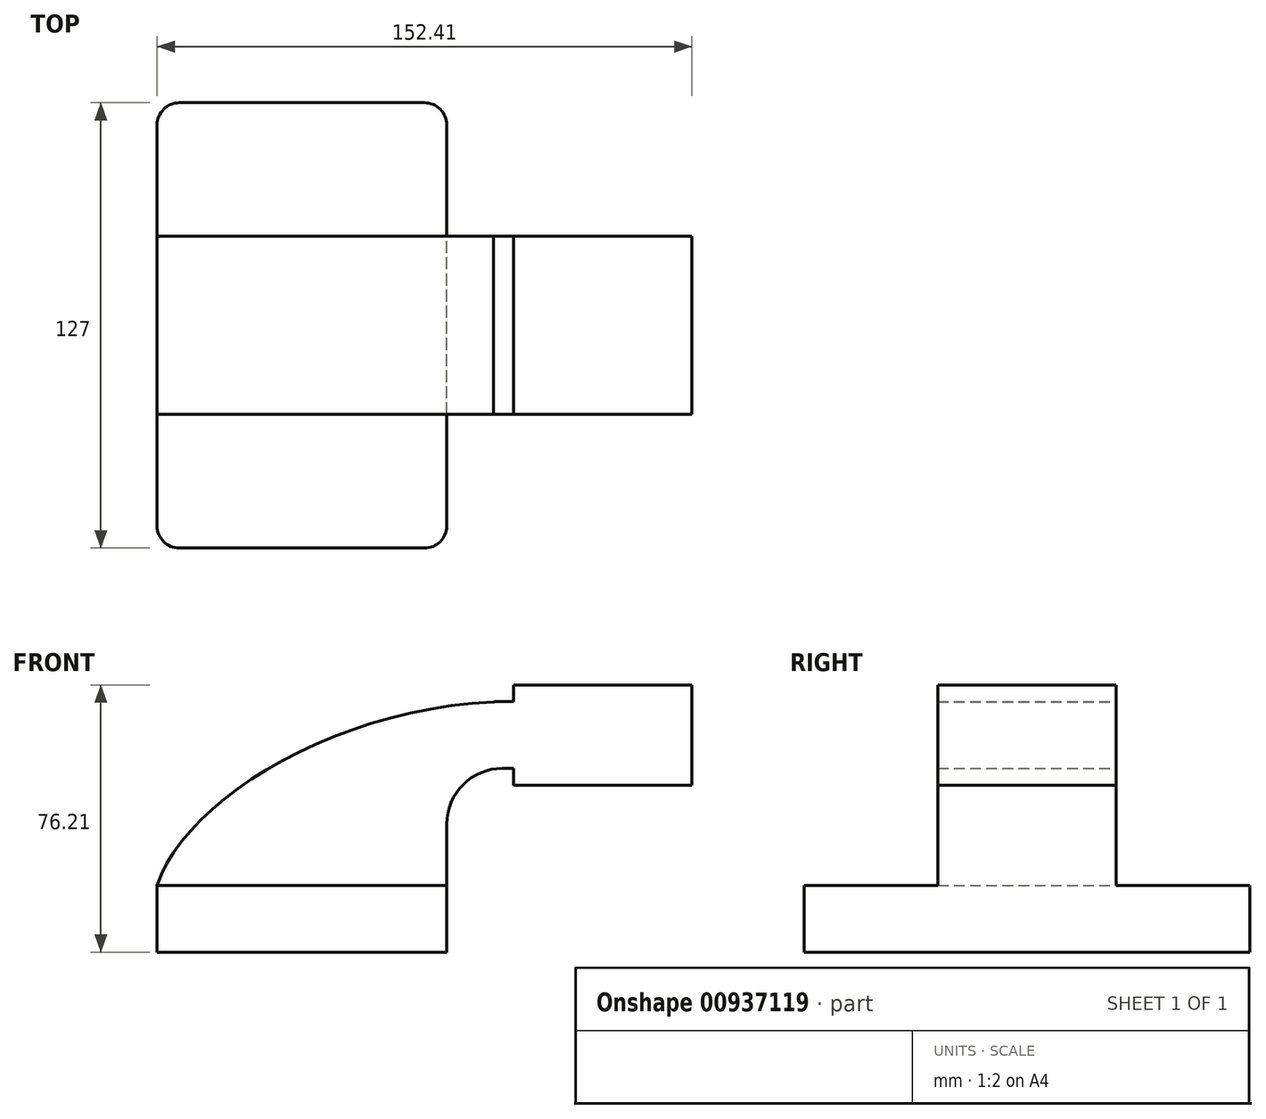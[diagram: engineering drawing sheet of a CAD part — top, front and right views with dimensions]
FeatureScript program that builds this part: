
annotation { "Feature Type Name" : "Feature", "Feature Type Description" : "" }
export const myFeature = defineFeature(function(context is Context, id is Id, definition is map)
    precondition{}
    {
        {
            var Q0;
            Q0=qCreatedBy(makeId("Front.planeOp"),FACE);
            var sketch = newSketch(context, id + "F0", { "sketchPlane" : qUnion([Q0])});
            skLineSegment(sketch, "E0.bottom", {"start": v(-41.28, -9.53) * mm, "end": v(41.28, -9.53) * mm});
            skLineSegment(sketch, "E0.top", {"start": v(-41.28, 9.53) * mm, "end": v(41.28, 9.53) * mm});
            skLineSegment(sketch, "E0.left", {"start": v(-41.28, -9.53) * mm, "end": v(-41.28, 9.53) * mm});
            skLineSegment(sketch, "E0.right", {"start": v(41.28, -9.53) * mm, "end": v(41.28, 9.53) * mm});
            skPoint(sketch, "E0.middle", {"position": v(0, 0) * mm});
            skLineSegment(sketch, "E1.bottom", {"start": v(60.33, 38.1) * mm, "end": v(111.12, 38.1) * mm});
            skLineSegment(sketch, "E1.top", {"start": v(60.33, 66.67) * mm, "end": v(111.12, 66.67) * mm});
            skLineSegment(sketch, "E1.left", {"start": v(60.33, 38.1) * mm, "end": v(60.33, 66.67) * mm});
            skLineSegment(sketch, "E1.right", {"start": v(111.12, 38.1) * mm, "end": v(111.12, 66.67) * mm});
            skPoint(sketch, "E1.middle", {"position": v(85.72, 52.39) * mm});
            skLineSegment(sketch, "E2", {"start": v(41.28, 9.53) * mm, "end": v(41.28, 27) * mm});
            skArc(sketch, "E3", {"start": v(41.27, 27) * mm, "mid": v(45.92, 38.23) * mm, "end": v(57.15, 42.88) * mm});
            skLineSegment(sketch, "E4", {"start": v(57.15, 42.88) * mm, "end": v(86.97, 42.88) * mm});
            skLineSegment(sketch, "E5.0", {"start": v(57.15, 61.93) * mm, "end": v(86.97, 61.93) * mm});
            skArc(sketch, "E5.1", {"start": v(22.23, 27) * mm, "mid": v(32.45, 51.7) * mm, "end": v(57.15, 61.93) * mm});
            skLineSegment(sketch, "E5.2", {"start": v(22.22, 9.53) * mm, "end": v(22.22, 27) * mm});
            skLineSegment(sketch, "E6", {"start": v(86.97, 38.1) * mm, "end": v(86.97, 66.67) * mm});
            skPoint(sketch, "E6.startSnap0", {"position": v(85.72, 38.1) * mm});
            skFitSpline(sketch, "E7", {"points": [v(-41.28, 9.53) * mm, v(57.15, 61.93) * mm], "startDerivative": vector(23.8, 72.58) * mm, "endDerivative": vector(142.71, 3.96) * mm});
            skSolve(sketch);
        }
        {
            var Q0;
            Q0=makeQuery(id+"F0.imprint","IMPRINT",FACE,{"disambiguationData":[TD([[makeQuery(id+"F0.imprint","IMPRINT",EDGE,{"derivedFrom":sQuery(id+"F0.wireOp",EDGE,"E0.bottom")}),1.0]])]});
            extrude(context, id + "F1", {"entities" : qUnion([Q0]), "endBound" : BoundingType.SYMMETRIC, "depth" : 127 * mm, "offsetDistance" : 25.4 * mm});
        }
        {
            var Q0;
            {var subQ1=sQuery(id+"F0.wireOp",EDGE,"E2");Q0=makeQuery(id+"F0.imprint","IMPRINT",FACE,{"disambiguationData":[TD([[makeQuery(id+"F0.imprint","IMPRINT",EDGE,{"derivedFrom":subQ1}),1.0]])]});}
            var Q1;
            {var subQ0=sQuery(id+"F0.wireOp",EDGE,"E4");var subQ1=sQuery(id+"F0.wireOp",EDGE,"E1.left");var subQ2=makeQuery(id+"F0.imprint","INTERSECT",VERTEX,{"derivedFrom":[subQ1,subQ0]});Q1=makeQuery(id+"F0.imprint","IMPRINT",FACE,{"disambiguationData":[TD([[makeQuery(id+"F0.imprint","IMPRINT",EDGE,{"disambiguationData":[TD([[subQ2,-1.0]])],"derivedFrom":subQ1}),-1.0]])]});}
            extrude(context, id + "F2", {"entities" : qUnion([Q0, Q1]), "operationType" : NewBodyOperationType.ADD, "endBound" : BoundingType.SYMMETRIC, "depth" : 50.8 * mm, "offsetDistance" : 25.4 * mm});
        }
        {
            var Q0;
            {var subQ3=sQuery(id+"F0.wireOp",EDGE,"E5.2");Q0=makeQuery(id+"F0.imprint","IMPRINT",FACE,{"disambiguationData":[TD([[makeQuery(id+"F0.imprint","IMPRINT",EDGE,{"derivedFrom":subQ3}),1.0]])]});}
            extrude(context, id + "F3", {"entities" : qUnion([Q0]), "operationType" : NewBodyOperationType.ADD, "endBound" : BoundingType.SYMMETRIC, "depth" : 15.88 * mm, "offsetDistance" : 25.4 * mm});
        }
        {
            var Q0;
            {var subQ4=sQuery(id+"F0.wireOp",EDGE,"E1.right");Q0=makeQuery(id+"F0.imprint","IMPRINT",FACE,{"disambiguationData":[TD([[makeQuery(id+"F0.imprint","IMPRINT",EDGE,{"derivedFrom":subQ4}),1.0]])]});}
            var Q1;
            Q1=sQuery(id+"F0.wireOp",EDGE,"E6");
            revolve(context, id + "F4", {"operationType" : NewBodyOperationType.ADD, "surfaceOperationType" : NewSurfaceOperationType.NEW, "entities" : qUnion([Q0]), "axis" : qUnion([Q1]), "revolveType" : RevolveType.FULL});
        }
        {
            var Q0;
            Q0=makeQuery(id+"F1.opExtrude","CAP_EDGE",EDGE,{"disambiguationData":[OSD([sQuery(id+"F0.wireOp",EDGE,"E0.left")])],"isStart":false});
            var Q1;
            Q1=makeQuery(id+"F1.opExtrude","CAP_EDGE",EDGE,{"disambiguationData":[OSD([sQuery(id+"F0.wireOp",EDGE,"E0.right")])],"isStart":false});
            var Q2;
            Q2=makeQuery(id+"F1.opExtrude","CAP_EDGE",EDGE,{"disambiguationData":[OSD([sQuery(id+"F0.wireOp",EDGE,"E0.right")])],"isStart":true});
            var Q3;
            Q3=makeQuery(id+"F1.opExtrude","CAP_EDGE",EDGE,{"disambiguationData":[OSD([sQuery(id+"F0.wireOp",EDGE,"E0.left")])],"isStart":true});
            fillet(context, id + "F5", {"entities" : qUnion([Q0, Q1, Q2, Q3]), "radius" : 6.35 * mm, "tangentPropagation" : true, "allowEdgeOverflow" : false});
        }
        {
            var Q0;
            Q0 = qSketchRegion(id + "F0", true);
            extrude(context, id + "F6", {"entities" : qUnion([Q0]), "operationType" : NewBodyOperationType.ADD, "endBound" : BoundingType.SYMMETRIC, "depth" : 50.8 * mm, "offsetDistance" : 25.4 * mm});
        }
    });
